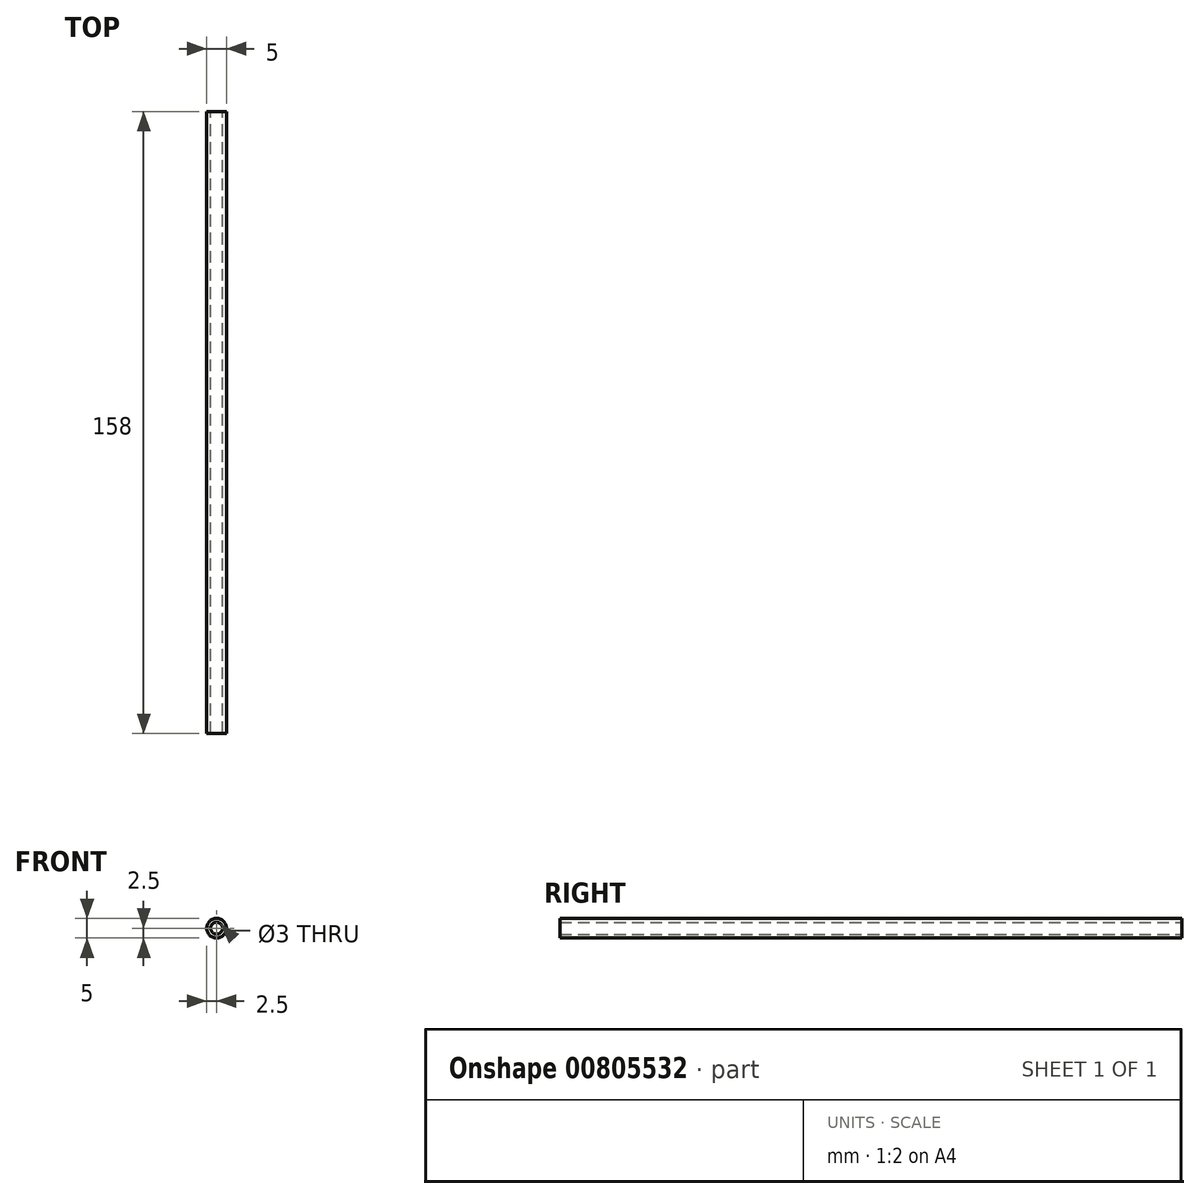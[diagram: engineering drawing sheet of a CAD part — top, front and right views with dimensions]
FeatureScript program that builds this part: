
annotation { "Feature Type Name" : "Feature", "Feature Type Description" : "" }
export const myFeature = defineFeature(function(context is Context, id is Id, definition is map)
    precondition{}
    {
        {
            var Q0;
            Q0=qCreatedBy(makeId("Front.planeOp"),FACE);
            var sketch = newSketch(context, id + "F0", { "sketchPlane" : qUnion([Q0])});
            skCircle(sketch, "E0", {"center": v(0, 0) * mm, "radius": 2.5 * mm});
            skCircle(sketch, "E1", {"center": v(0, 0) * mm, "radius": 1.5 * mm});
            skSolve(sketch);
        }
        {
            var Q0;
            Q0=makeQuery(id+"F0.imprint","IMPRINT",FACE,{"disambiguationData":[TD([[makeQuery(id+"F0.imprint","IMPRINT",EDGE,{"derivedFrom":sQuery(id+"F0.wireOp",EDGE,"E0")}),1.0]])]});
            extrude(context, id + "F1", {"entities" : qUnion([Q0]), "depth" : 158 * mm, "offsetDistance" : 25 * mm, "symmetric" : true});
        }
    });
